# Revit family: Faucet-Lavatory-KOHLER-Aleo-K-72298IN_1
name_source: partatom
category: Plumbing Fixtures
revit_build: Autodesk Revit 2017 (Build: 20160225_1515(x64)
units: mm (PartAtom-declared; Revit-internal decimal feet)

## family parameters
Cut with Voids When Loaded = No
Host = Face
OmniClass Number = 23.31.11.00
OmniClass Title = Faucets
Part Type = Normal
Room Calculation Point = No
Round Connector Dimension = Use Diameter
Shared = No

## types (4) — shared parameters
ADA Compliant = No
Assembly Code = D2010
CW Connection = Yes
Cold Water Inlet = Cold Water Inlet
Date Modified = 10/07/2020
Default Elevation = 36"
Flow Rate = 2 GPM
HW Connection = Yes
Handle Clearance = 3 9/16"
Height = 10 9/16"
Hot Water Inlet = Hot Water Inlet
Length = 6 5/16"
Manufacturer = KOHLER Co.
Master Format 2014 = 22 41 39
Master Format 2014 Name = Residential Faucets, Supplies, and Trim
Material = Premium Metal Construction
Pressure = 60.00 psi
Product Documentation Link = http://resources.kohler.com
Product Name = Aleo
Product Page URL = https://www.kohler.co.in
Spout Reach = 6 5/16"
URL = https://www.kohler.co.in
Vent Connection = No
Waste Connection = No
Waste Water Outlet = Waste Water Outlet
WaterSense Certified = No
Width = 2"

## per-type parameters (varying)
| type | Description | Drain Included | Finish | Model | Type |
| With Drain, CP-Polished Chrome | Tall lavatory faucet | Yes | Kohler-Metal-CP-Polished_Chrome | K-72298IN-4-CP | 1 |
| Without Drain, CP-Polished Chrome | Tall lavatory faucet without drain | No | Kohler-Metal-CP-Polished_Chrome | K-72298IN-4ND-CP | 2 |
| Without Drain, RGD-Polished Rose Gold | Tall lavatory faucet without drain | No | Kohler-Metal-RGD-Polished_Rose_Gold | K-72298IN-4ND-RGD | 3 |
| Without Drain, BV-Brushed Bronze | Tall lavatory faucet without drain | No | Kohler-Metal-BV-Brushed_Bronze | K-72298IN-4ND-BV | 4 |

## geometry (parser evidence)
native form markers: Sweep x5
no freeform markers — native parametric forms only
